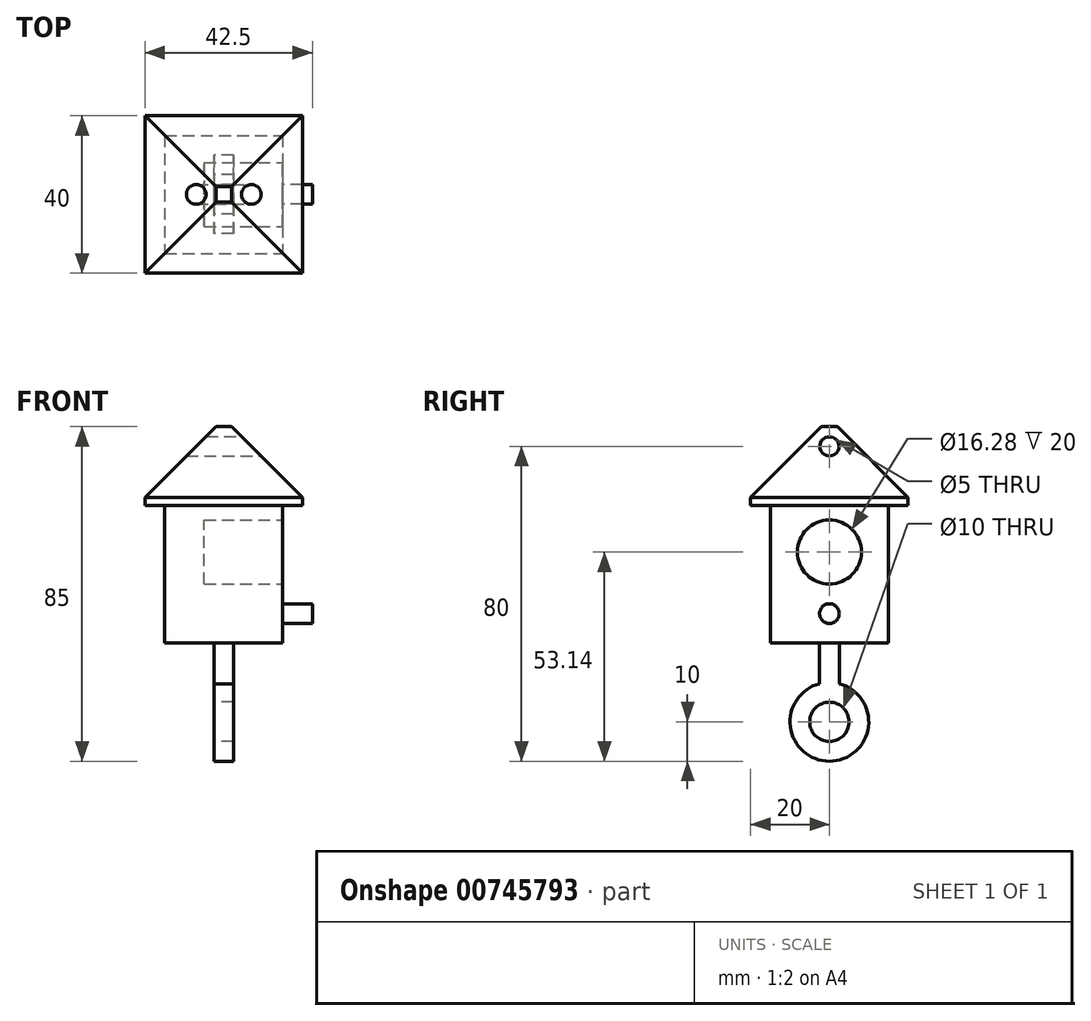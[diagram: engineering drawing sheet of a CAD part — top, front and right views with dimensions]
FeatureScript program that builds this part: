
annotation { "Feature Type Name" : "Feature", "Feature Type Description" : "" }
export const myFeature = defineFeature(function(context is Context, id is Id, definition is map)
    precondition{}
    {
        {
            var Q0;
            Q0=qCreatedBy(makeId("Top.planeOp"),FACE);
            var sketch = newSketch(context, id + "F0", { "sketchPlane" : qUnion([Q0])});
            skLineSegment(sketch, "E0.bottom", {"start": v(-15, 15) * mm, "end": v(15, 15) * mm});
            skLineSegment(sketch, "E0.top", {"start": v(-15, -15) * mm, "end": v(15, -15) * mm});
            skLineSegment(sketch, "E0.left", {"start": v(-15, 15) * mm, "end": v(-15, -15) * mm});
            skLineSegment(sketch, "E0.right", {"start": v(15, 15) * mm, "end": v(15, -15) * mm});
            skPoint(sketch, "E0.middle", {"position": v(0, 0) * mm});
            skSolve(sketch);
        }
        {
            var Q0;
            Q0 = qSketchRegion(id + "F0", true);
            extrude(context, id + "F1", {"entities" : qUnion([Q0]), "depth" : 35 * mm, "offsetDistance" : 25.4 * mm});
        }
        {
            var Q0;
            Q0=makeQuery(id+"F1.opExtrude","CAP_FACE",FACE,{"disambiguationData":[OSD([sQuery(id+"F0.wireOp",EDGE,"E0.bottom"),sQuery(id+"F0.wireOp",EDGE,"E0.top"),sQuery(id+"F0.wireOp",EDGE,"E0.left"),sQuery(id+"F0.wireOp",EDGE,"E0.right")])],"isStart":false});
            var sketch = newSketch(context, id + "F2", { "sketchPlane" : qUnion([Q0])});
            skLineSegment(sketch, "E1.bottom", {"start": v(20, 20) * mm, "end": v(-20, 20) * mm});
            skLineSegment(sketch, "E1.top", {"start": v(20, -20) * mm, "end": v(-20, -20) * mm});
            skLineSegment(sketch, "E1.left", {"start": v(20, 20) * mm, "end": v(20, -20) * mm});
            skLineSegment(sketch, "E1.right", {"start": v(-20, 20) * mm, "end": v(-20, -20) * mm});
            skPoint(sketch, "E1.middle", {"position": v(0, 0) * mm});
            skSolve(sketch);
        }
        {
            var Q0;
            Q0 = qSketchRegion(id + "F2", true);
            extrude(context, id + "F3", {"entities" : qUnion([Q0]), "operationType" : NewBodyOperationType.ADD, "depth" : 20 * mm, "offsetDistance" : 25.4 * mm});
        }
        {
            var Q0;
            Q0=makeQuery(id+"F3.opExtrude","CAP_EDGE",EDGE,{"disambiguationData":[OSD([sQuery(id+"F2.wireOp",EDGE,"E1.left")])],"isStart":false});
            var Q1;
            Q1=makeQuery(id+"F3.opExtrude","CAP_EDGE",EDGE,{"disambiguationData":[OSD([sQuery(id+"F2.wireOp",EDGE,"E1.bottom")])],"isStart":false});
            var Q2;
            Q2=makeQuery(id+"F3.opExtrude","CAP_EDGE",EDGE,{"disambiguationData":[OSD([sQuery(id+"F2.wireOp",EDGE,"E1.right")])],"isStart":false});
            var Q3;
            Q3=makeQuery(id+"F3.opExtrude","CAP_FACE",FACE,{"disambiguationData":[OSD([sQuery(id+"F2.wireOp",EDGE,"E1.bottom"),sQuery(id+"F2.wireOp",EDGE,"E1.top"),sQuery(id+"F2.wireOp",EDGE,"E1.left"),sQuery(id+"F2.wireOp",EDGE,"E1.right")])],"isStart":false});
            chamfer(context, id + "F4", {"entities" : qUnion([Q0, Q1, Q2, Q3]), "width" : 18 * mm, "tangentPropagation" : true});
        }
        {
            var Q0;
            Q0=makeQuery(id+"F1.opExtrude","SWEPT_FACE",FACE,{"disambiguationData":[OSD([sQuery(id+"F0.wireOp",EDGE,"E0.right")])]});
            var sketch = newSketch(context, id + "F5", { "sketchPlane" : qUnion([Q0])});
            skCircle(sketch, "E2", {"center": v(0, 23.14) * mm, "radius": 8.14 * mm});
            skPoint(sketch, "E2.first.point", {"position": v(-5.35, 17) * mm});
            skPoint(sketch, "E2.second.point", {"position": v(5, 16.72) * mm});
            skPoint(sketch, "E2.third.point", {"position": v(0, 31.28) * mm});
            skSolve(sketch);
        }
        {
            var Q0;
            Q0 = qSketchRegion(id + "F5", true);
            var Q1;
            Q1=sQuery(id+"F5.wireOp",EDGE,"E2");
            extrude(context, id + "F6", {"entities" : qUnion([Q0]), "operationType" : NewBodyOperationType.REMOVE, "surfaceOperationType" : NewSurfaceOperationType.ADD, "surfaceEntities" : qUnion([Q1]), "oppositeDirection" : true, "depth" : 20 * mm, "offsetDistance" : 25.4 * mm});
        }
        {
            var Q0;
            Q0=makeQuery(id+"F1.opExtrude","SWEPT_FACE",FACE,{"disambiguationData":[OSD([sQuery(id+"F0.wireOp",EDGE,"E0.right")])]});
            var sketch = newSketch(context, id + "F7", { "sketchPlane" : qUnion([Q0])});
            skCircle(sketch, "E3", {"center": v(0, 7.5) * mm, "radius": 2.5 * mm});
            skSolve(sketch);
        }
        {
            var Q0;
            Q0=makeQuery(id+"F7.imprint","IMPRINT",FACE,{"disambiguationData":[TD([[makeQuery(id+"F7.imprint","IMPRINT",EDGE,{"derivedFrom":sQuery(id+"F7.wireOp",EDGE,"E3")}),1.0]])]});
            var Q1;
            Q1 = qSketchRegion(id + "F9", true);
            extrude(context, id + "F8", {"entities" : qUnion([Q0, Q1]), "operationType" : NewBodyOperationType.ADD, "depth" : 7.5 * mm, "offsetDistance" : 25.4 * mm});
        }
        {
            var Q0;
            Q0=makeQuery(id+"F3.opExtrude","SWEPT_FACE",FACE,{"disambiguationData":[OSD([sQuery(id+"F2.wireOp",EDGE,"E1.left")])]});
            var sketch = newSketch(context, id + "F9", { "sketchPlane" : qUnion([Q0])});
            skCircle(sketch, "E4", {"center": v(0, 50) * mm, "radius": 2.5 * mm});
            skSolve(sketch);
        }
        {
            var Q0;
            Q0=makeQuery(id+"F9.imprint","IMPRINT",FACE,{"disambiguationData":[TD([[makeQuery(id+"F9.imprint","IMPRINT",EDGE,{"derivedFrom":sQuery(id+"F9.wireOp",EDGE,"E4")}),1.0]])]});
            extrude(context, id + "F10", {"entities" : qUnion([Q0]), "operationType" : NewBodyOperationType.REMOVE, "oppositeDirection" : true, "depth" : 79.5 * mm, "offsetDistance" : 25.4 * mm});
        }
        {
            var Q0;
            Q0=makeQuery(id+"F1.opExtrude","CAP_FACE",FACE,{"disambiguationData":[OSD([sQuery(id+"F0.wireOp",EDGE,"E0.bottom"),sQuery(id+"F0.wireOp",EDGE,"E0.top"),sQuery(id+"F0.wireOp",EDGE,"E0.left"),sQuery(id+"F0.wireOp",EDGE,"E0.right")])],"isStart":true});
            var sketch = newSketch(context, id + "F11", { "sketchPlane" : qUnion([Q0])});
            skLineSegment(sketch, "E5.bottom", {"start": v(2.5, 2.5) * mm, "end": v(-2.5, 2.5) * mm});
            skLineSegment(sketch, "E5.top", {"start": v(2.5, -2.5) * mm, "end": v(-2.5, -2.5) * mm});
            skLineSegment(sketch, "E5.left", {"start": v(2.5, 2.5) * mm, "end": v(2.5, -2.5) * mm});
            skLineSegment(sketch, "E5.right", {"start": v(-2.5, 2.5) * mm, "end": v(-2.5, -2.5) * mm});
            skPoint(sketch, "E5.middle", {"position": v(0, 0) * mm});
            skSolve(sketch);
        }
        {
            var Q0;
            Q0=makeQuery(id+"F11.imprint","IMPRINT",FACE,{"disambiguationData":[TD([[makeQuery(id+"F11.imprint","IMPRINT",EDGE,{"derivedFrom":sQuery(id+"F11.wireOp",EDGE,"E5.bottom")}),1.0]])]});
            extrude(context, id + "F12", {"entities" : qUnion([Q0]), "operationType" : NewBodyOperationType.ADD, "depth" : 15 * mm, "offsetDistance" : 25.4 * mm});
        }
        {
            var Q0;
            Q0=qCreatedBy(makeId("Right.planeOp"),FACE);
            var sketch = newSketch(context, id + "F13", { "sketchPlane" : qUnion([Q0])});
            skCircle(sketch, "E6", {"center": v(0, -20) * mm, "radius": 5 * mm});
            skCircle(sketch, "E7", {"center": v(0, -20) * mm, "radius": 10 * mm});
            skSolve(sketch);
        }
        {
            var Q0;
            Q0=makeQuery(id+"F13.imprint","IMPRINT",FACE,{"disambiguationData":[TD([[makeQuery(id+"F13.imprint","IMPRINT",EDGE,{"derivedFrom":sQuery(id+"F13.wireOp",EDGE,"E6")}),-1.0]])]});
            extrude(context, id + "F14", {"entities" : qUnion([Q0]), "operationType" : NewBodyOperationType.ADD, "endBound" : BoundingType.SYMMETRIC, "depth" : 5 * mm, "offsetDistance" : 25.4 * mm});
        }
    });
